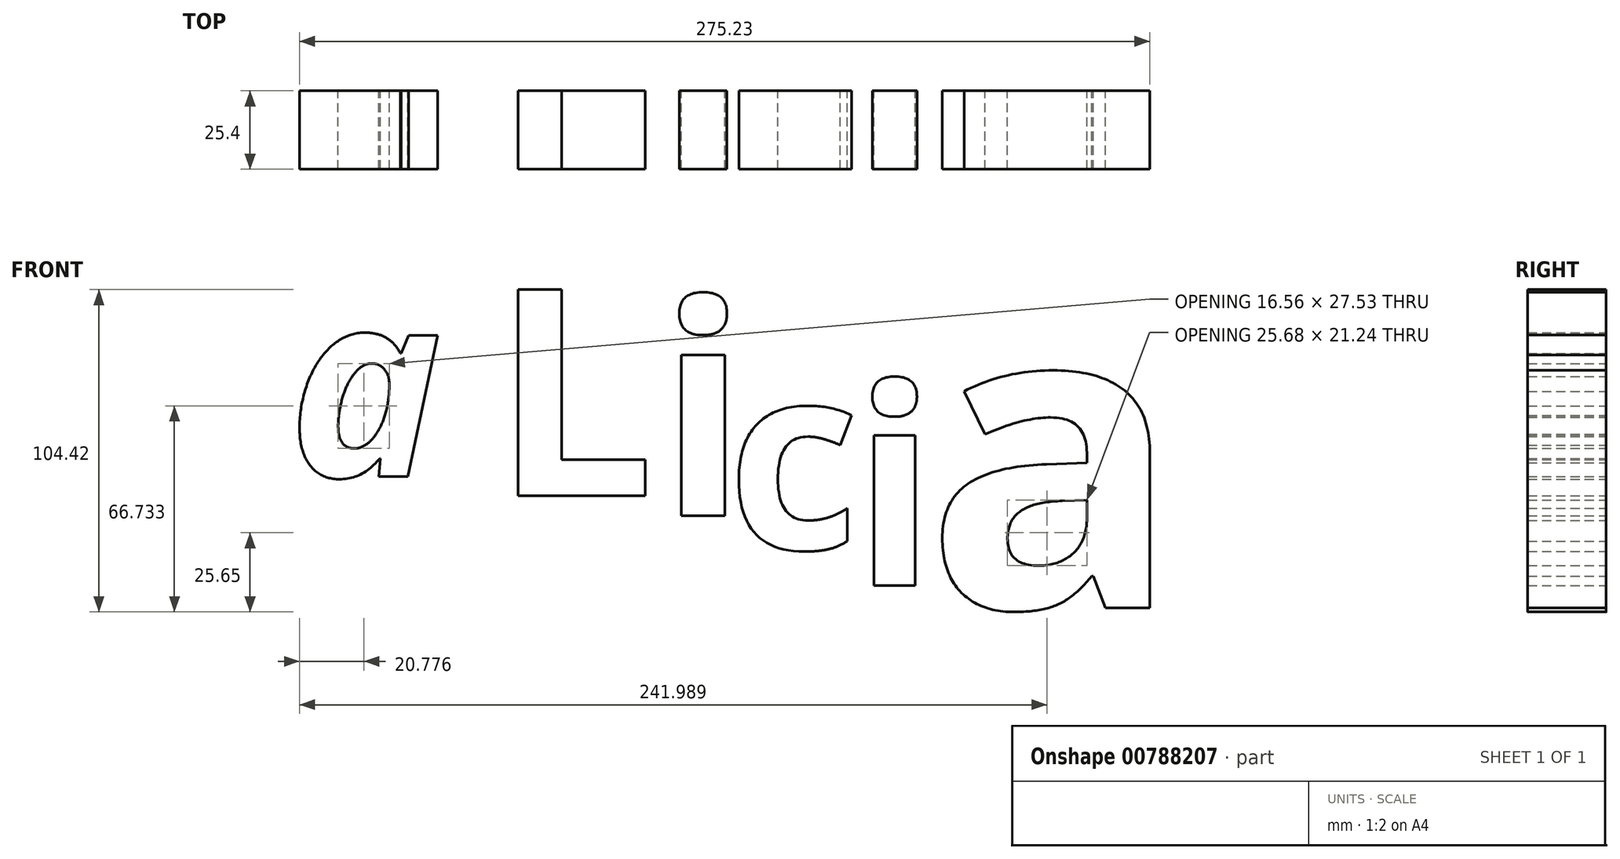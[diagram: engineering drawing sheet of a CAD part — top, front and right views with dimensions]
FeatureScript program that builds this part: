
annotation { "Feature Type Name" : "Feature", "Feature Type Description" : "" }
export const myFeature = defineFeature(function(context is Context, id is Id, definition is map)
    precondition{}
    {
        {
            var Q0;
            Q0=qCreatedBy(makeId("Front.planeOp"),FACE);
            var sketch = newSketch(context, id + "F0", { "sketchPlane" : qUnion([Q0])});
            skText(sketch, "E0", { "text": "a", "fontName": "OpenSans-BoldItalic.ttf"});
            const initialGuessF0  = {"E0": [-0.21746, -0.03664, 1, 0, 0.06041]};
            skSetInitialGuess(sketch, initialGuessF0);
            skSolve(sketch);
        }
        {
            var Q0;
            Q0=qCreatedBy(makeId("Front.planeOp"),FACE);
            var sketch = newSketch(context, id + "F1", { "sketchPlane" : qUnion([Q0])});
            skText(sketch, "E1", { "text": "L", "fontName": "OpenSans-Bold.ttf"});
            const initialGuessF1  = {"E1": [-0.15149, -0.04284, 1, 0, 0.06736]};
            skSetInitialGuess(sketch, initialGuessF1);
            skSolve(sketch);
        }
        {
            var Q0;
            Q0=qCreatedBy(makeId("Front.planeOp"),FACE);
            var sketch = newSketch(context, id + "F2", { "sketchPlane" : qUnion([Q0])});
            skText(sketch, "E2", { "text": "i", "fontName": "OpenSans-Bold.ttf"});
            const initialGuessF2  = {"E2": [-0.0977, -0.04926, 1, 0, 0.06857]};
            skSetInitialGuess(sketch, initialGuessF2);
            skSolve(sketch);
        }
        {
            var Q0;
            Q0 = qSketchRegion(id + "F2", true);
            extrude(context, id + "F3", {"entities" : qUnion([Q0]), "depth" : 25.4 * mm, "offsetDistance" : 25.4 * mm});
        }
        {
            var Q0;
            Q0=qCreatedBy(makeId("Front.planeOp"),FACE);
            var sketch = newSketch(context, id + "F4", { "sketchPlane" : qUnion([Q0])});
            skText(sketch, "E3", { "text": "c", "fontName": "OpenSans-Bold.ttf"});
            const initialGuessF4  = {"E3": [-0.07536, -0.06007, 1, 0, 0.06007]};
            skSetInitialGuess(sketch, initialGuessF4);
            skSolve(sketch);
        }
        {
            var Q0;
            Q0 = qSketchRegion(id + "F4", true);
            extrude(context, id + "F5", {"entities" : qUnion([Q0]), "depth" : 25.4 * mm, "offsetDistance" : 25.4 * mm});
        }
        {
            var Q0;
            Q0=qCreatedBy(makeId("Front.planeOp"),FACE);
            var sketch = newSketch(context, id + "F6", { "sketchPlane" : qUnion([Q0])});
            skText(sketch, "E4", { "text": "i", "fontName": "OpenSans-Bold.ttf"});
            const initialGuessF6  = {"E4": [-0.03477, -0.07187, 1, 0, 0.0641]};
            skSetInitialGuess(sketch, initialGuessF6);
            skSolve(sketch);
        }
        {
            var Q0;
            Q0=qCreatedBy(makeId("Front.planeOp"),FACE);
            var sketch = newSketch(context, id + "F7", { "sketchPlane" : qUnion([Q0])});
            skText(sketch, "E5", { "text": "a", "fontName": "OpenSans-Bold.ttf"});
            const initialGuessF7  = {"E5": [-0.01152, -0.07911, 1, 0, 0.09936]};
            skSetInitialGuess(sketch, initialGuessF7);
            skSolve(sketch);
        }
        {
            var Q0;
            Q0 = qSketchRegion(id + "F7", true);
            extrude(context, id + "F8", {"entities" : qUnion([Q0]), "depth" : 25.4 * mm, "offsetDistance" : 25.4 * mm});
        }
        {
            var Q0;
            Q0 = qSketchRegion(id + "F1", true);
            extrude(context, id + "F9", {"entities" : qUnion([Q0]), "depth" : 25.4 * mm, "offsetDistance" : 25.4 * mm});
        }
        {
            var Q0;
            Q0=makeQuery(id+"F0.imprint","IMPRINT",FACE,{"disambiguationData":[TD([[makeQuery(id+"F0.imprint","IMPRINT",EDGE,{"derivedFrom":sQuery(id+"F0.wireOp",EDGE,"E0.sketch_text.stroke-0")}),-1.0]])]});
            extrude(context, id + "F10", {"entities" : qUnion([Q0]), "depth" : 25.4 * mm, "offsetDistance" : 25.4 * mm});
        }
        {
            var Q0;
            Q0 = qSketchRegion(id + "F6", true);
            extrude(context, id + "F11", {"entities" : qUnion([Q0]), "depth" : 25.4 * mm, "offsetDistance" : 25.4 * mm});
        }
    });
